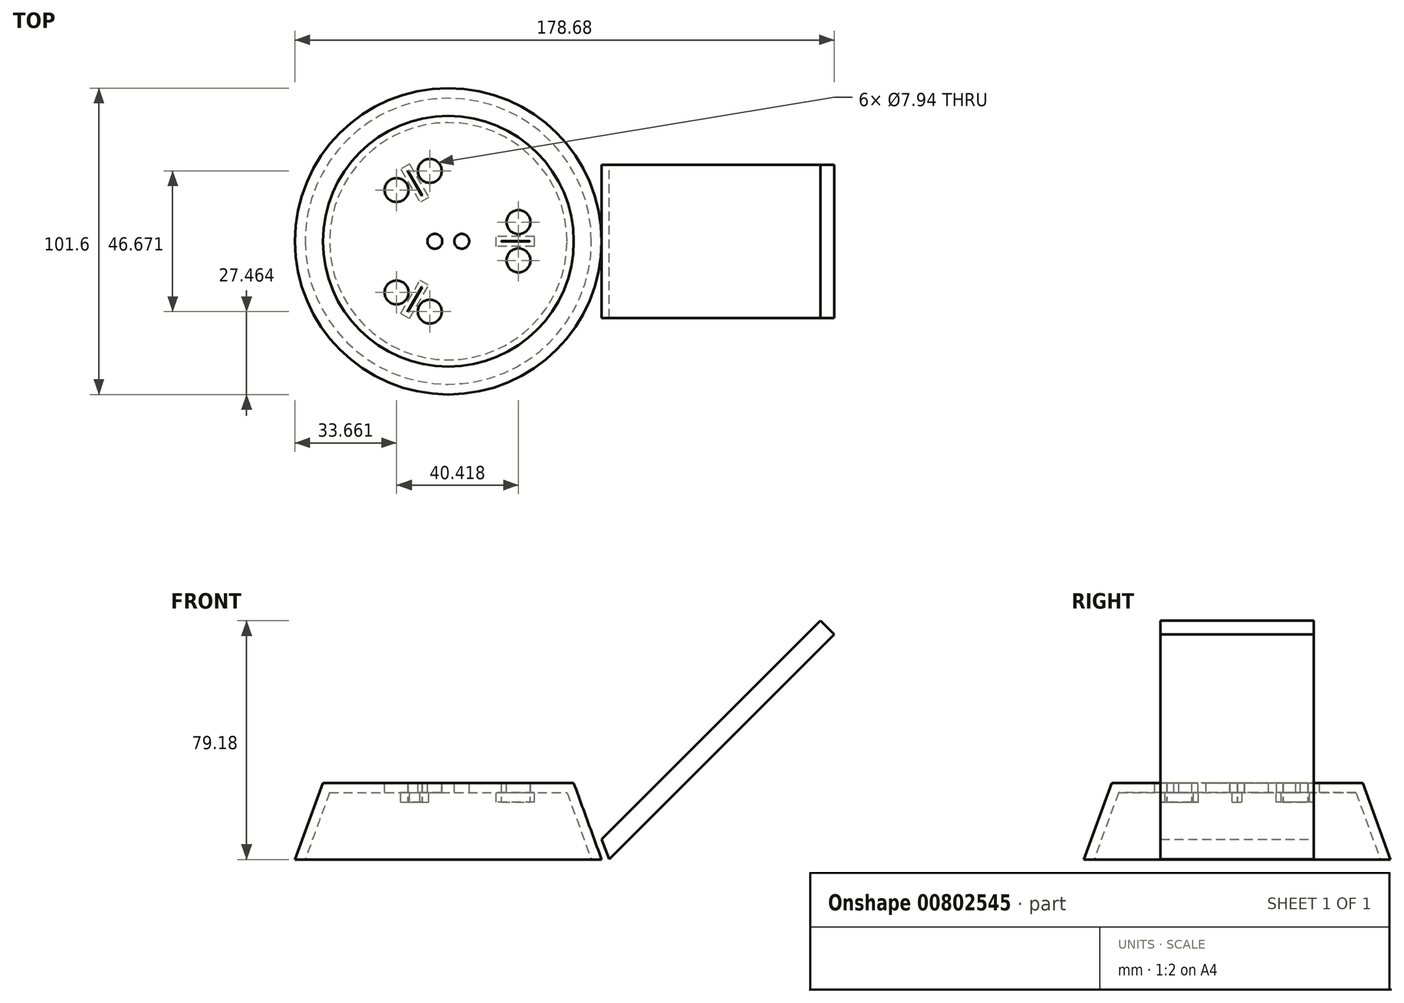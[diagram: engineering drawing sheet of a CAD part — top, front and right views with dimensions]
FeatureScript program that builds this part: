
annotation { "Feature Type Name" : "Feature", "Feature Type Description" : "" }
export const myFeature = defineFeature(function(context is Context, id is Id, definition is map)
    precondition{}
    {
        {
            var Q0;
            Q0=qCreatedBy(makeId("Front.planeOp"),FACE);
            var sketch = newSketch(context, id + "F0", { "sketchPlane" : qUnion([Q0])});
            skLineSegment(sketch, "E0", {"start": v(41.55, 69.52) * mm, "end": v(48.37, 50.8) * mm});
            skLineSegment(sketch, "E1", {"start": v(0, 53.57) * mm, "end": v(0, 0) * mm});
            skLineSegment(sketch, "E2", {"start": v(41.55, 69.52) * mm, "end": v(0, 69.52) * mm});
            skLineSegment(sketch, "E3", {"start": v(0, 69.52) * mm, "end": v(0, 44.12) * mm});
            skLineSegment(sketch, "E4", {"start": v(0, 44.12) * mm, "end": v(50.8, 44.12) * mm});
            skLineSegment(sketch, "E5", {"start": v(48.37, 50.8) * mm, "end": v(50.8, 44.12) * mm});
            skSolve(sketch);
        }
        {
            var Q0;
            Q0=makeQuery(id+"F0.imprint","IMPRINT",FACE,{"disambiguationData":[TD([[makeQuery(id+"F0.imprint","IMPRINT",EDGE,{"derivedFrom":sQuery(id+"F0.wireOp",EDGE,"E0")}),-1.0]])]});
            var Q1;
            {var subQ0=sQuery(id+"F0.wireOp",EDGE,"onV8PMYQ-VyxF-B8O7-HB0v-HSfoXODMd58i");Q1=makeQuery(id+"F0.imprint","IMPRINT",FACE,{"disambiguationData":[TD([[makeQuery(id+"F0.imprint","IMPRINT",EDGE,{"derivedFrom":subQ0}),-1.0]])]});}
            var Q2;
            Q2=sQuery(id+"F0.wireOp",EDGE,"E1");
            revolve(context, id + "F1", {"surfaceOperationType" : NewSurfaceOperationType.NEW, "entities" : qUnion([Q0, Q1]), "axis" : qUnion([Q2]), "revolveType" : RevolveType.FULL});
        }
        {
            var Q0;
            Q0=qCreatedBy(makeId("Front.planeOp"),FACE);
            var sketch = newSketch(context, id + "F2", { "sketchPlane" : qUnion([Q0])});
            skLineSegment(sketch, "E6.0", {"start": v(127.88, 118.72) * mm, "end": v(53.3, 44.14) * mm});
            skLineSegment(sketch, "E6.1", {"start": v(50.8, 50.8) * mm, "end": v(123.3, 123.3) * mm});
            skLineSegment(sketch, "E6.2", {"start": v(123.3, 123.3) * mm, "end": v(127.88, 118.72) * mm});
            skPoint(sketch, "E6.3", {"position": v(125.59, 121) * mm});
            skLineSegment(sketch, "E7", {"start": v(50.8, 50.8) * mm, "end": v(53.3, 44.14) * mm});
            skSolve(sketch);
        }
        {
            var Q0;
            Q0=makeQuery(id+"F2.imprint","IMPRINT",FACE,{"disambiguationData":[TD([[makeQuery(id+"F2.imprint","IMPRINT",EDGE,{"derivedFrom":sQuery(id+"F2.wireOp",EDGE,"E6.0")}),-1.0]])]});
            extrude(context, id + "F3", {"entities" : qUnion([Q0]), "depth" : 25.4 * mm, "offsetDistance" : 25.4 * mm, "hasSecondDirection" : true, "secondDirectionOppositeDirection" : true, "secondDirectionDepth" : 25.4 * mm});
        }
        {
            var Q0;
            Q0=makeQuery(id+"F1.opRevolve","SWEPT_FACE",FACE,{"disambiguationData":[OSD([sQuery(id+"F0.wireOp",EDGE,"E4")])]});
            shell(context, id + "F4", {"entities" : qUnion([Q0]), "thickness" : 3.17 * mm});
        }
        {
            var Q0;
            Q0=makeQuery(id+"F1.opRevolve","SWEPT_FACE",FACE,{"disambiguationData":[OSD([sQuery(id+"F0.wireOp",EDGE,"E2")])]});
            var sketch = newSketch(context, id + "F5", { "sketchPlane" : qUnion([Q0])});
            skCircle(sketch, "E8", {"center": v(-4.46, 0) * mm, "radius": 2.47 * mm});
            skCircle(sketch, "E9", {"center": v(4.47, 0) * mm, "radius": 2.47 * mm});
            skSolve(sketch);
        }
        {
            var Q0;
            Q0=qSketchRegion(id+"F5",true);
            extrude(context, id + "F6", {"entities" : qUnion([Q0]), "operationType" : NewBodyOperationType.REMOVE, "endBound" : BoundingType.UP_TO_NEXT, "oppositeDirection" : true, "depth" : 25.4 * mm, "offsetDistance" : 25.4 * mm});
        }
        {
            var Q0;
            Q0=makeQuery(id+"F1.opRevolve","SWEPT_FACE",FACE,{"disambiguationData":[OSD([sQuery(id+"F0.wireOp",EDGE,"E2")])]});
            var sketch = newSketch(context, id + "F7", { "sketchPlane" : qUnion([Q0])});
            skLineSegment(sketch, "E10", {"start": v(0, 0) * mm, "end": v(-20.78, 35.99) * mm, "construction": true});
            skLineSegment(sketch, "E11", {"start": v(0, 0) * mm, "end": v(41.55, 0) * mm, "construction": true});
            skLineSegment(sketch, "E12", {"start": v(0, 0) * mm, "end": v(-20.78, -35.99) * mm, "construction": true});
            skCircle(sketch, "E13", {"center": v(0, 0) * mm, "radius": 24.13 * mm, "construction": true});
            skCircle(sketch, "E14", {"center": v(-6.14, -23.34) * mm, "radius": 3.97 * mm});
            skCircle(sketch, "E15", {"center": v(-17.14, -16.99) * mm, "radius": 3.97 * mm});
            skCircle(sketch, "E16.1.0", {"center": v(23.28, -6.35) * mm, "radius": 3.97 * mm});
            skCircle(sketch, "E16.1.1", {"center": v(23.28, 6.35) * mm, "radius": 3.97 * mm});
            skCircle(sketch, "E16.2.0", {"center": v(-6.14, 23.34) * mm, "radius": 3.97 * mm});
            skCircle(sketch, "E16.2.1", {"center": v(-17.14, 16.99) * mm, "radius": 3.97 * mm});
            skSolve(sketch);
        }
        {
            var Q0;
            Q0=makeQuery(id+"F7.imprint","IMPRINT",FACE,{"disambiguationData":[TD([[makeQuery(id+"F7.imprint","IMPRINT",EDGE,{"derivedFrom":sQuery(id+"F7.wireOp",EDGE,"RapGbSY8-IpOW-W7Cr-I6qc-ZG4xxbcdLVoa")}),1.0]])]});
            var Q1;
            Q1=makeQuery(id+"F7.imprint","IMPRINT",FACE,{"disambiguationData":[TD([[makeQuery(id+"F7.imprint","IMPRINT",EDGE,{"derivedFrom":sQuery(id+"F7.wireOp",EDGE,"IGuVjlWC-YWjh-J5nc-Mawc-mcWyPe0ibYVq")}),1.0]])]});
            var Q2;
            Q2=makeQuery(id+"F7.imprint","IMPRINT",FACE,{"disambiguationData":[TD([[makeQuery(id+"F7.imprint","IMPRINT",EDGE,{"derivedFrom":sQuery(id+"F7.wireOp",EDGE,"F3LzENUP-gJWh-AGhM-4yzn-LWY1Z7Q8ePyD")}),1.0]])]});
            var Q3;
            Q3=makeQuery(id+"F7.imprint","IMPRINT",FACE,{"disambiguationData":[TD([[makeQuery(id+"F7.imprint","IMPRINT",EDGE,{"derivedFrom":sQuery(id+"F7.wireOp",EDGE,"3u7ExzTy-9fGH-4HWB-yVm0-lmGXTGqtbzzD")}),1.0]])]});
            var Q4;
            Q4=makeQuery(id+"F7.imprint","IMPRINT",FACE,{"disambiguationData":[TD([[makeQuery(id+"F7.imprint","IMPRINT",EDGE,{"derivedFrom":sQuery(id+"F7.wireOp",EDGE,"E14")}),1.0]])]});
            var Q5;
            Q5=makeQuery(id+"F7.imprint","IMPRINT",FACE,{"disambiguationData":[TD([[makeQuery(id+"F7.imprint","IMPRINT",EDGE,{"derivedFrom":sQuery(id+"F7.wireOp",EDGE,"E15")}),1.0]])]});
            var Q6;
            Q6=makeQuery(id+"F7.imprint","IMPRINT",FACE,{"disambiguationData":[TD([[makeQuery(id+"F7.imprint","IMPRINT",EDGE,{"derivedFrom":sQuery(id+"F7.wireOp",EDGE,"E16.2.1")}),1.0]])]});
            var Q7;
            Q7=makeQuery(id+"F7.imprint","IMPRINT",FACE,{"disambiguationData":[TD([[makeQuery(id+"F7.imprint","IMPRINT",EDGE,{"derivedFrom":sQuery(id+"F7.wireOp",EDGE,"E16.2.0")}),1.0]])]});
            var Q8;
            Q8=makeQuery(id+"F7.imprint","IMPRINT",FACE,{"disambiguationData":[TD([[makeQuery(id+"F7.imprint","IMPRINT",EDGE,{"derivedFrom":sQuery(id+"F7.wireOp",EDGE,"E16.1.1")}),1.0]])]});
            var Q9;
            Q9=makeQuery(id+"F7.imprint","IMPRINT",FACE,{"disambiguationData":[TD([[makeQuery(id+"F7.imprint","IMPRINT",EDGE,{"derivedFrom":sQuery(id+"F7.wireOp",EDGE,"E16.1.0")}),1.0]])]});
            extrude(context, id + "F8", {"entities" : qUnion([Q0, Q1, Q2, Q3, Q4, Q5, Q6, Q7, Q8, Q9]), "operationType" : NewBodyOperationType.REMOVE, "endBound" : BoundingType.UP_TO_NEXT, "oppositeDirection" : true, "depth" : 25.4 * mm, "offsetDistance" : 25.4 * mm});
        }
        {
            var Q0;
            Q0=makeQuery(id+"F4.opShell","OFFSET_FACE",FACE,{"disambiguationData":[OSD([sQuery(id+"F0.wireOp",EDGE,"E2")])]});
            var sketch = newSketch(context, id + "F9", { "sketchPlane" : qUnion([Q0])});
            skLineSegment(sketch, "E17", {"start": v(1.4, 0) * mm, "end": v(77.6, 0) * mm, "construction": true});
            skLineSegment(sketch, "E18.bottom", {"start": v(28.58, 1.65) * mm, "end": v(15.88, 1.65) * mm});
            skLineSegment(sketch, "E18.top", {"start": v(28.58, -1.65) * mm, "end": v(15.88, -1.65) * mm});
            skLineSegment(sketch, "E18.left", {"start": v(28.57, 1.65) * mm, "end": v(28.57, -1.65) * mm});
            skLineSegment(sketch, "E18.right", {"start": v(15.88, 1.65) * mm, "end": v(15.88, -1.65) * mm});
            skLineSegment(sketch, "E19.1.0", {"start": v(-12.86, 25.57) * mm, "end": v(-6.5, 14.57) * mm});
            skLineSegment(sketch, "E19.1.1", {"start": v(-9.37, 12.92) * mm, "end": v(-6.5, 14.57) * mm});
            skLineSegment(sketch, "E19.1.2", {"start": v(-15.72, 23.92) * mm, "end": v(-9.37, 12.92) * mm});
            skLineSegment(sketch, "E19.1.3", {"start": v(-15.72, 23.92) * mm, "end": v(-12.86, 25.57) * mm});
            skLineSegment(sketch, "E19.2.0", {"start": v(-15.72, -23.92) * mm, "end": v(-9.37, -12.92) * mm});
            skLineSegment(sketch, "E19.2.1", {"start": v(-6.5, -14.57) * mm, "end": v(-9.37, -12.92) * mm});
            skLineSegment(sketch, "E19.2.2", {"start": v(-12.86, -25.57) * mm, "end": v(-6.5, -14.57) * mm});
            skLineSegment(sketch, "E19.2.3", {"start": v(-12.86, -25.57) * mm, "end": v(-15.72, -23.92) * mm});
            skPoint(sketch, "E19.center", {"position": v(0, 0) * mm});
            skSolve(sketch);
        }
        {
            var Q0;
            Q0=makeQuery(id+"F9.imprint","IMPRINT",FACE,{"disambiguationData":[TD([[makeQuery(id+"F9.imprint","IMPRINT",EDGE,{"derivedFrom":sQuery(id+"F9.wireOp",EDGE,"E18.bottom")}),1.0]])]});
            var Q1;
            Q1=makeQuery(id+"F9.imprint","IMPRINT",FACE,{"disambiguationData":[TD([[makeQuery(id+"F9.imprint","IMPRINT",EDGE,{"derivedFrom":sQuery(id+"F9.wireOp",EDGE,"E19.1.0")}),-1.0]])]});
            var Q2;
            Q2=makeQuery(id+"F9.imprint","IMPRINT",FACE,{"disambiguationData":[TD([[makeQuery(id+"F9.imprint","IMPRINT",EDGE,{"derivedFrom":sQuery(id+"F9.wireOp",EDGE,"E19.2.0")}),-1.0]])]});
            extrude(context, id + "F10", {"entities" : qUnion([Q0, Q1, Q2]), "operationType" : NewBodyOperationType.ADD, "depth" : 3.17 * mm, "offsetDistance" : 25.4 * mm});
        }
        {
            var Q0;
            Q0=makeQuery(id+"F10.opExtrude","CAP_FACE",FACE,{"disambiguationData":[OSD([sQuery(id+"F9.wireOp",EDGE,"E19.2.0"),sQuery(id+"F9.wireOp",EDGE,"E19.2.1"),sQuery(id+"F9.wireOp",EDGE,"E19.2.2"),sQuery(id+"F9.wireOp",EDGE,"E19.2.3")])],"isStart":false});
            var sketch = newSketch(context, id + "F11", { "sketchPlane" : qUnion([Q0])});
            skLineSegment(sketch, "E20.0", {"start": v(41.55, 0) * mm, "end": v(0, 0) * mm, "construction": true});
            skLineSegment(sketch, "E21", {"start": v(17.48, 0.05) * mm, "end": v(26.97, 0.05) * mm});
            skLineSegment(sketch, "E22", {"start": v(26.97, 0.05) * mm, "end": v(26.97, -0.05) * mm});
            skLineSegment(sketch, "E23", {"start": v(26.97, -0.05) * mm, "end": v(17.48, -0.05) * mm});
            skLineSegment(sketch, "E24", {"start": v(17.48, -0.05) * mm, "end": v(17.48, 0.05) * mm});
            skLineSegment(sketch, "E25.1.0", {"start": v(-13.44, 23.39) * mm, "end": v(-8.7, 15.16) * mm});
            skLineSegment(sketch, "E25.1.1", {"start": v(-8.7, 15.16) * mm, "end": v(-8.78, 15.1) * mm});
            skLineSegment(sketch, "E25.1.2", {"start": v(-8.78, 15.1) * mm, "end": v(-13.53, 23.34) * mm});
            skLineSegment(sketch, "E25.1.3", {"start": v(-13.53, 23.34) * mm, "end": v(-13.44, 23.39) * mm});
            skLineSegment(sketch, "E25.2.0", {"start": v(-13.53, -23.34) * mm, "end": v(-8.78, -15.1) * mm});
            skLineSegment(sketch, "E25.2.1", {"start": v(-8.78, -15.1) * mm, "end": v(-8.7, -15.16) * mm});
            skLineSegment(sketch, "E25.2.2", {"start": v(-8.7, -15.16) * mm, "end": v(-13.44, -23.39) * mm});
            skLineSegment(sketch, "E25.2.3", {"start": v(-13.44, -23.39) * mm, "end": v(-13.53, -23.34) * mm});
            skPoint(sketch, "E25.center", {"position": v(0, 0) * mm});
            skSolve(sketch);
        }
        {
            var Q0;
            Q0=makeQuery(id+"F11.imprint","IMPRINT",FACE,{"disambiguationData":[TD([[makeQuery(id+"F11.imprint","IMPRINT",EDGE,{"derivedFrom":sQuery(id+"F11.wireOp",EDGE,"E21")}),-1.0]])]});
            var Q1;
            Q1=makeQuery(id+"F11.imprint","IMPRINT",FACE,{"disambiguationData":[TD([[makeQuery(id+"F11.imprint","IMPRINT",EDGE,{"derivedFrom":sQuery(id+"F11.wireOp",EDGE,"E25.2.0")}),-1.0]])]});
            var Q2;
            Q2=makeQuery(id+"F11.imprint","IMPRINT",FACE,{"disambiguationData":[TD([[makeQuery(id+"F11.imprint","IMPRINT",EDGE,{"derivedFrom":sQuery(id+"F11.wireOp",EDGE,"E25.1.0")}),-1.0]])]});
            extrude(context, id + "F12", {"entities" : qUnion([Q0, Q1, Q2]), "operationType" : NewBodyOperationType.REMOVE, "oppositeDirection" : true, "depth" : 25.4 * mm, "offsetDistance" : 25.4 * mm});
        }
    });
